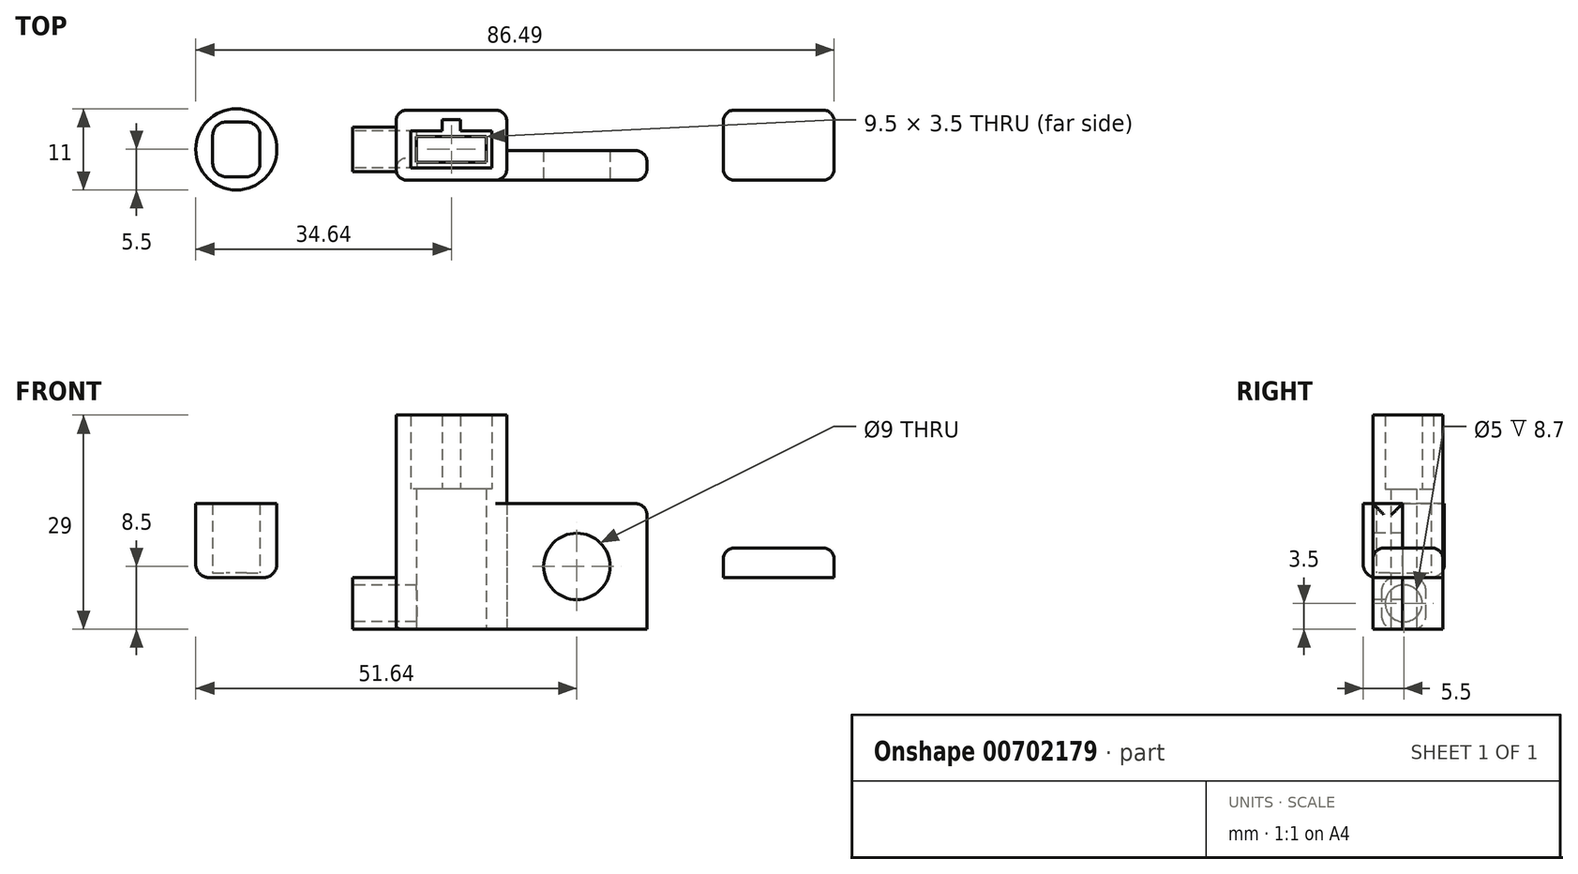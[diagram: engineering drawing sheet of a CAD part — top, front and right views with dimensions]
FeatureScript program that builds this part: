
annotation { "Feature Type Name" : "Feature", "Feature Type Description" : "" }
export const myFeature = defineFeature(function(context is Context, id is Id, definition is map)
    precondition{}
    {
        {
            var Q0;
            Q0=qCreatedBy(makeId("Top.planeOp"),FACE);
            var sketch = newSketch(context, id + "F0", { "sketchPlane" : qUnion([Q0])});
            skPoint(sketch, "E0.middle", {"position": v(0, 0) * mm});
            skLineSegment(sketch, "E1.bottom", {"start": v(5.5, -2.5) * mm, "end": v(-5.5, -2.5) * mm});
            skLineSegment(sketch, "E1.top", {"start": v(5.5, 2.5) * mm, "end": v(1.25, 2.5) * mm});
            skLineSegment(sketch, "E1.left", {"start": v(5.5, -2.5) * mm, "end": v(5.5, 2.5) * mm});
            skLineSegment(sketch, "E1.right", {"start": v(-5.5, -2.5) * mm, "end": v(-5.5, 2.5) * mm});
            skLineSegment(sketch, "E2.top", {"start": v(1.25, 4.01) * mm, "end": v(-1.25, 4.01) * mm});
            skLineSegment(sketch, "E2.left", {"start": v(1.25, 2.5) * mm, "end": v(1.25, 4.01) * mm});
            skLineSegment(sketch, "E2.right", {"start": v(-1.25, 2.5) * mm, "end": v(-1.25, 4.01) * mm});
            skPoint(sketch, "E2.middle", {"position": v(0, 3.26) * mm});
            skPoint(sketch, "E2.middle.positionSnap0", {"position": v(0, 2.5) * mm});
            skPoint(sketch, "E2.centerSnap0", {"position": v(0, 2.5) * mm});
            skLineSegment(sketch, "E3.bottom", {"start": v(7.5, -4.18) * mm, "end": v(-7.5, -4.18) * mm});
            skLineSegment(sketch, "E3.top", {"start": v(7.5, 5.32) * mm, "end": v(-7.5, 5.32) * mm});
            skLineSegment(sketch, "E3.left", {"start": v(7.5, -4.18) * mm, "end": v(7.5, 5.32) * mm});
            skLineSegment(sketch, "E3.right", {"start": v(-7.5, -4.18) * mm, "end": v(-7.5, 5.32) * mm});
            skPoint(sketch, "E3.middle", {"position": v(0, 0.57) * mm});
            skLineSegment(sketch, "E4.trimOffspring", {"start": v(-1.25, 2.5) * mm, "end": v(-5.5, 2.5) * mm});
            skLineSegment(sketch, "E5.bottom", {"start": v(4.75, -1.75) * mm, "end": v(-4.75, -1.75) * mm});
            skLineSegment(sketch, "E5.top", {"start": v(4.75, 1.75) * mm, "end": v(-4.75, 1.75) * mm});
            skLineSegment(sketch, "E5.left", {"start": v(4.75, -1.75) * mm, "end": v(4.75, 1.75) * mm});
            skLineSegment(sketch, "E5.right", {"start": v(-4.75, -1.75) * mm, "end": v(-4.75, 1.75) * mm});
            skLineSegment(sketch, "E6.bottom", {"start": v(7.5, -4.18) * mm, "end": v(26.5, -4.18) * mm});
            skLineSegment(sketch, "E6.top", {"start": v(7.5, -0.18) * mm, "end": v(26.5, -0.18) * mm});
            skLineSegment(sketch, "E6.left", {"start": v(7.5, -4.18) * mm, "end": v(7.5, -0.18) * mm});
            skLineSegment(sketch, "E6.right", {"start": v(26.5, -4.18) * mm, "end": v(26.5, -0.18) * mm});
            skLineSegment(sketch, "E7.bottom", {"start": v(-7.5, 3) * mm, "end": v(-13.37, 3) * mm});
            skLineSegment(sketch, "E7.top", {"start": v(-7.5, -3) * mm, "end": v(-13.37, -3) * mm});
            skLineSegment(sketch, "E7.left", {"start": v(-7.5, 3) * mm, "end": v(-7.5, -3) * mm});
            skLineSegment(sketch, "E7.right", {"start": v(-13.37, 3) * mm, "end": v(-13.37, -3) * mm});
            skPoint(sketch, "E7.middle", {"position": v(-10.43, 0) * mm});
            skSolve(sketch);
        }
        {
            var Q0;
            Q0=makeQuery(id+"F0.imprint","IMPRINT",FACE,{"disambiguationData":[TD([[makeQuery(id+"F0.imprint","IMPRINT",EDGE,{"derivedFrom":sQuery(id+"F0.wireOp",EDGE,"E1.bottom")}),1.0]])]});
            extrude(context, id + "F1", {"entities" : qUnion([Q0]), "depth" : 22 * mm, "offsetDistance" : 25 * mm});
        }
        {
            var Q0;
            Q0=makeQuery(id+"F0.imprint","IMPRINT",FACE,{"disambiguationData":[TD([[makeQuery(id+"F0.imprint","IMPRINT",EDGE,{"derivedFrom":sQuery(id+"F0.wireOp",EDGE,"E1.bottom")}),-1.0]])]});
            extrude(context, id + "F2", {"entities" : qUnion([Q0]), "operationType" : NewBodyOperationType.ADD, "depth" : 12 * mm, "offsetDistance" : 25 * mm});
        }
        {
            var Q0;
            Q0=makeQuery(id+"F0.imprint","IMPRINT",FACE,{"disambiguationData":[TD([[makeQuery(id+"F0.imprint","IMPRINT",EDGE,{"derivedFrom":sQuery(id+"F0.wireOp",EDGE,"E6.bottom")}),1.0]])]});
            extrude(context, id + "F3", {"entities" : qUnion([Q0]), "operationType" : NewBodyOperationType.ADD, "depth" : 10 * mm, "offsetDistance" : 25 * mm});
        }
        {
            var Q0;
            {var subQ0=sQuery(id+"F0.wireOp",EDGE,"E6.left");var subQ1=sQuery(id+"F0.wireOp",EDGE,"E4.trimOffspring");var subQ2=sQuery(id+"F0.wireOp",EDGE,"E2.right");var subQ3=sQuery(id+"F0.wireOp",EDGE,"E2.left");var subQ4=sQuery(id+"F0.wireOp",EDGE,"E2.top");var subQ5=sQuery(id+"F0.wireOp",EDGE,"E1.right");var subQ6=sQuery(id+"F0.wireOp",EDGE,"E1.left");var subQ7=sQuery(id+"F0.wireOp",EDGE,"E1.top");var subQ8=sQuery(id+"F0.wireOp",EDGE,"E1.bottom");Q0=makeQuery(id+"F3.boolean.opBoolean","MERGE",FACE,{"derivedFrom":[makeQuery(id+"F2.boolean.opBoolean","MERGE",FACE,{"derivedFrom":[makeQuery(id+"F1.opExtrude","CAP_FACE",FACE,{"disambiguationData":[OSD([subQ8,subQ7,subQ6,subQ5,subQ4,subQ3,subQ2,sQuery(id+"F0.wireOp",EDGE,"E3.bottom"),sQuery(id+"F0.wireOp",EDGE,"E3.top"),sQuery(id+"F0.wireOp",EDGE,"E3.left"),sQuery(id+"F0.wireOp",EDGE,"E3.right"),subQ1,subQ0])],"isStart":true}),makeQuery(id+"F2.opExtrude","CAP_FACE",FACE,{"disambiguationData":[OSD([subQ8,subQ7,subQ6,subQ5,subQ4,subQ3,subQ2,subQ1,sQuery(id+"F0.wireOp",EDGE,"E5.bottom"),sQuery(id+"F0.wireOp",EDGE,"E5.top"),sQuery(id+"F0.wireOp",EDGE,"E5.left"),sQuery(id+"F0.wireOp",EDGE,"E5.right")])],"isStart":true})]}),makeQuery(id+"F3.opExtrude","CAP_FACE",FACE,{"disambiguationData":[OSD([sQuery(id+"F0.wireOp",EDGE,"E6.bottom"),sQuery(id+"F0.wireOp",EDGE,"E6.top"),subQ0,sQuery(id+"F0.wireOp",EDGE,"E6.right")])],"isStart":true})]});}
            extrude(context, id + "F4", {"entities" : qUnion([Q0]), "operationType" : NewBodyOperationType.ADD, "depth" : 7 * mm, "offsetDistance" : 25 * mm});
        }
        {
            var Q0;
            Q0=makeQuery(id+"F3.boolean.opBoolean","MERGE",FACE,{"derivedFrom":[makeQuery(id+"F1.opExtrude","SWEPT_FACE",FACE,{"disambiguationData":[OSD([sQuery(id+"F0.wireOp",EDGE,"E3.bottom")])]}),makeQuery(id+"F3.opExtrude","SWEPT_FACE",FACE,{"disambiguationData":[OSD([sQuery(id+"F0.wireOp",EDGE,"E6.bottom")])]})]});
            var sketch = newSketch(context, id + "F5", { "sketchPlane" : qUnion([Q0])});
            skCircle(sketch, "E8", {"center": v(17, 1.5) * mm, "radius": 4.5 * mm});
            skPoint(sketch, "E8.centerSnap0", {"position": v(17, 10) * mm});
            skPoint(sketch, "E8.centerSnap1", {"position": v(23, 1.5) * mm});
            skPoint(sketch, "E9", {"position": v(26.5, 1.5) * mm});
            skSolve(sketch);
        }
        {
            var Q0;
            Q0=makeQuery(id+"F5.imprint","IMPRINT",FACE,{"disambiguationData":[TD([[makeQuery(id+"F5.imprint","IMPRINT",EDGE,{"derivedFrom":sQuery(id+"F5.wireOp",EDGE,"E8")}),1.0]])]});
            extrude(context, id + "F6", {"entities" : qUnion([Q0]), "operationType" : NewBodyOperationType.REMOVE, "oppositeDirection" : true, "depth" : 25 * mm, "offsetDistance" : 25 * mm});
        }
        {
            var Q0;
            Q0=makeQuery(id+"F0.imprint","IMPRINT",FACE,{"disambiguationData":[TD([[makeQuery(id+"F0.imprint","IMPRINT",EDGE,{"derivedFrom":sQuery(id+"F0.wireOp",EDGE,"E7.bottom")}),1.0]])]});
            extrude(context, id + "F7", {"entities" : qUnion([Q0]), "operationType" : NewBodyOperationType.ADD, "oppositeDirection" : true, "depth" : 7 * mm, "offsetDistance" : 25 * mm});
        }
        {
            var Q0;
            Q0=makeQuery(id+"F1.opExtrude","SWEPT_EDGE",EDGE,{"disambiguationData":[OSD([sQuery(id+"F0.wireOp",EDGE,"E3.top"),sQuery(id+"F0.wireOp",EDGE,"E3.right")])]});
            var Q1;
            Q1=makeQuery(id+"F1.opExtrude","SWEPT_EDGE",EDGE,{"disambiguationData":[OSD([sQuery(id+"F0.wireOp",EDGE,"E3.top"),sQuery(id+"F0.wireOp",EDGE,"E3.left")])]});
            var Q2;
            Q2=makeQuery(id+"F1.opExtrude","SWEPT_EDGE",EDGE,{"disambiguationData":[OSD([sQuery(id+"F0.wireOp",EDGE,"E3.bottom"),sQuery(id+"F0.wireOp",EDGE,"E3.left")])]});
            var Q3;
            Q3=makeQuery(id+"F1.opExtrude","SWEPT_EDGE",EDGE,{"disambiguationData":[OSD([sQuery(id+"F0.wireOp",EDGE,"E3.bottom"),sQuery(id+"F0.wireOp",EDGE,"E3.right")])]});
            var Q4;
            Q4=makeQuery(id+"F1.opExtrude","SWEPT_EDGE",EDGE,{"disambiguationData":[OSD([sQuery(id+"F0.wireOp",EDGE,"E3.bottom"),sQuery(id+"F0.wireOp",EDGE,"E6.bottom"),sQuery(id+"F0.wireOp",EDGE,"E6.left")])]});
            var Q5;
            Q5=makeQuery(id+"F3.opExtrude","SWEPT_EDGE",EDGE,{"disambiguationData":[OSD([sQuery(id+"F0.wireOp",EDGE,"E6.bottom"),sQuery(id+"F0.wireOp",EDGE,"E6.right")])]});
            var Q6;
            Q6=makeQuery(id+"F3.opExtrude","SWEPT_EDGE",EDGE,{"disambiguationData":[OSD([sQuery(id+"F0.wireOp",EDGE,"E6.top"),sQuery(id+"F0.wireOp",EDGE,"E6.right")])]});
            var Q7;
            Q7=makeQuery(id+"F3.opExtrude","SWEPT_EDGE",EDGE,{"disambiguationData":[OSD([sQuery(id+"F0.wireOp",EDGE,"E3.left"),sQuery(id+"F0.wireOp",EDGE,"E6.top"),sQuery(id+"F0.wireOp",EDGE,"E6.left")])]});
            var Q8;
            Q8=makeQuery(id+"F3.opExtrude","CAP_EDGE",EDGE,{"disambiguationData":[OSD([sQuery(id+"F0.wireOp",EDGE,"E6.right")])],"isStart":false});
            fillet(context, id + "F8", {"entities" : qUnion([Q0, Q1, Q2, Q3, Q4, Q5, Q6, Q7, Q8]), "radius" : 1.5 * mm, "tangentPropagation" : true, "allowEdgeOverflow" : false});
        }
        {
            var Q0;
            Q0=makeQuery(id+"F7.opExtrude","CAP_EDGE",EDGE,{"disambiguationData":[OSD([sQuery(id+"F0.wireOp",EDGE,"E7.bottom")])],"isStart":false});
            var Q1;
            Q1=makeQuery(id+"F7.opExtrude","CAP_EDGE",EDGE,{"disambiguationData":[OSD([sQuery(id+"F0.wireOp",EDGE,"E7.top")])],"isStart":false});
            var Q2;
            Q2=makeQuery(id+"F7.opExtrude","CAP_EDGE",EDGE,{"disambiguationData":[OSD([sQuery(id+"F0.wireOp",EDGE,"E7.top")])],"isStart":true});
            var Q3;
            Q3=makeQuery(id+"F7.opExtrude","CAP_EDGE",EDGE,{"disambiguationData":[OSD([sQuery(id+"F0.wireOp",EDGE,"E7.bottom")])],"isStart":true});
            fillet(context, id + "F9", {"entities" : qUnion([Q0, Q1, Q2, Q3]), "radius" : 1.8 * mm, "tangentPropagation" : true, "allowEdgeOverflow" : false});
        }
        {
            var Q0;
            Q0=makeQuery(id+"F7.opExtrude","SWEPT_FACE",FACE,{"disambiguationData":[OSD([sQuery(id+"F0.wireOp",EDGE,"E7.right")])]});
            var sketch = newSketch(context, id + "F10", { "sketchPlane" : qUnion([Q0])});
            skCircle(sketch, "E10", {"center": v(0, -3.5) * mm, "radius": 2.5 * mm});
            skPoint(sketch, "E10.centerSnap0", {"position": v(3, -3.5) * mm});
            skPoint(sketch, "E10.centerSnap1", {"position": v(0, -7) * mm});
            skSolve(sketch);
        }
        {
            var Q0;
            Q0=makeQuery(id+"F10.imprint","IMPRINT",FACE,{"disambiguationData":[TD([[makeQuery(id+"F10.imprint","IMPRINT",EDGE,{"derivedFrom":sQuery(id+"F10.wireOp",EDGE,"E10")}),1.0]])]});
            extrude(context, id + "F11", {"entities" : qUnion([Q0]), "operationType" : NewBodyOperationType.REMOVE, "oppositeDirection" : true, "depth" : 8.7 * mm, "offsetDistance" : 25 * mm});
        }
        {
            var Q0;
            Q0=qCreatedBy(makeId("Top.planeOp"),FACE);
            var sketch = newSketch(context, id + "F12", { "sketchPlane" : qUnion([Q0])});
            skLineSegment(sketch, "E11.bottom", {"start": v(-25.94, -3.7) * mm, "end": v(-32.34, -3.7) * mm});
            skLineSegment(sketch, "E11.top", {"start": v(-25.94, 3.7) * mm, "end": v(-32.34, 3.7) * mm});
            skLineSegment(sketch, "E11.left", {"start": v(-25.94, -3.7) * mm, "end": v(-25.94, 3.7) * mm});
            skLineSegment(sketch, "E11.right", {"start": v(-32.34, -3.7) * mm, "end": v(-32.34, 3.7) * mm});
            skPoint(sketch, "E11.middle", {"position": v(-29.14, 0) * mm});
            skCircle(sketch, "E12", {"center": v(-29.14, 0) * mm, "radius": 5.5 * mm});
            skSolve(sketch);
        }
        {
            var Q0;
            Q0=makeQuery(id+"F12.imprint","IMPRINT",FACE,{"disambiguationData":[TD([[makeQuery(id+"F12.imprint","IMPRINT",EDGE,{"derivedFrom":sQuery(id+"F12.wireOp",EDGE,"E11.bottom")}),1.0]])]});
            extrude(context, id + "F13", {"entities" : qUnion([Q0]), "depth" : 10 * mm, "offsetDistance" : 25 * mm});
        }
        {
            var Q0;
            Q0=makeQuery(id+"F12.imprint","IMPRINT",FACE,{"disambiguationData":[TD([[makeQuery(id+"F12.imprint","IMPRINT",EDGE,{"derivedFrom":sQuery(id+"F12.wireOp",EDGE,"E11.bottom")}),-1.0]])]});
            extrude(context, id + "F14", {"entities" : qUnion([Q0]), "operationType" : NewBodyOperationType.ADD, "depth" : 0.6 * mm, "offsetDistance" : 25 * mm});
        }
        {
            var Q0;
            Q0=makeQuery(id+"F13.opExtrude","SWEPT_EDGE",EDGE,{"disambiguationData":[OSD([sQuery(id+"F12.wireOp",EDGE,"E11.top"),sQuery(id+"F12.wireOp",EDGE,"E11.left")])]});
            var Q1;
            Q1=makeQuery(id+"F13.opExtrude","SWEPT_EDGE",EDGE,{"disambiguationData":[OSD([sQuery(id+"F12.wireOp",EDGE,"E11.top"),sQuery(id+"F12.wireOp",EDGE,"E11.right")])]});
            var Q2;
            Q2=makeQuery(id+"F13.opExtrude","CAP_EDGE",EDGE,{"disambiguationData":[OSD([sQuery(id+"F12.wireOp",EDGE,"E12")])],"isStart":true});
            var Q3;
            Q3=makeQuery(id+"F13.opExtrude","SWEPT_EDGE",EDGE,{"disambiguationData":[OSD([sQuery(id+"F12.wireOp",EDGE,"E11.bottom"),sQuery(id+"F12.wireOp",EDGE,"E11.left")])]});
            var Q4;
            Q4=makeQuery(id+"F13.opExtrude","SWEPT_EDGE",EDGE,{"disambiguationData":[OSD([sQuery(id+"F12.wireOp",EDGE,"E11.bottom"),sQuery(id+"F12.wireOp",EDGE,"E11.right")])]});
            fillet(context, id + "F15", {"entities" : qUnion([Q0, Q1, Q2, Q3, Q4]), "radius" : 1.8 * mm, "tangentPropagation" : true, "allowEdgeOverflow" : false});
        }
        {
            var Q0;
            Q0=qCreatedBy(makeId("Top.planeOp"),FACE);
            var sketch = newSketch(context, id + "F16", { "sketchPlane" : qUnion([Q0])});
            skLineSegment(sketch, "E13.bottom", {"start": v(51.85, -4.18) * mm, "end": v(36.85, -4.18) * mm});
            skLineSegment(sketch, "E13.top", {"start": v(51.85, 5.32) * mm, "end": v(36.85, 5.32) * mm});
            skLineSegment(sketch, "E13.left", {"start": v(51.85, -4.18) * mm, "end": v(51.85, 5.32) * mm});
            skLineSegment(sketch, "E13.right", {"start": v(36.85, -4.18) * mm, "end": v(36.85, 5.32) * mm});
            skLineSegment(sketch, "E14.left", {"start": v(51.85, -4.18) * mm, "end": v(51.85, -0.18) * mm});
            skLineSegment(sketch, "E15.left", {"start": v(36.85, 3) * mm, "end": v(36.85, -3) * mm});
            skPoint(sketch, "E15.middle", {"position": v(33.92, 0) * mm});
            skSolve(sketch);
        }
        {
            var Q0;
            {var subQ1=sQuery(id+"F16.wireOp",EDGE,"E13.bottom");Q0=makeQuery(id+"F16.imprint","IMPRINT",FACE,{"disambiguationData":[TD([[makeQuery(id+"F16.imprint","IMPRINT",EDGE,{"derivedFrom":subQ1}),-1.0]])]});}
            extrude(context, id + "F17", {"entities" : qUnion([Q0]), "depth" : 4 * mm, "offsetDistance" : 25 * mm});
        }
        {
            var Q0;
            Q0=makeQuery(id+"F17.opExtrude","SWEPT_EDGE",EDGE,{"disambiguationData":[OSD([sQuery(id+"F16.wireOp",EDGE,"E13.bottom"),sQuery(id+"F16.wireOp",EDGE,"E14.left")])]});
            var Q1;
            Q1=makeQuery(id+"F17.opExtrude","SWEPT_EDGE",EDGE,{"disambiguationData":[OSD([sQuery(id+"F16.wireOp",EDGE,"E13.bottom"),sQuery(id+"F16.wireOp",EDGE,"E13.right")])]});
            var Q2;
            Q2=makeQuery(id+"F17.opExtrude","SWEPT_EDGE",EDGE,{"disambiguationData":[OSD([sQuery(id+"F16.wireOp",EDGE,"E13.top"),sQuery(id+"F16.wireOp",EDGE,"E13.right")])]});
            var Q3;
            Q3=makeQuery(id+"F17.opExtrude","SWEPT_EDGE",EDGE,{"disambiguationData":[OSD([sQuery(id+"F16.wireOp",EDGE,"E13.top"),sQuery(id+"F16.wireOp",EDGE,"E13.left")])]});
            var Q4;
            Q4=makeQuery(id+"F17.opExtrude","CAP_FACE",FACE,{"disambiguationData":[OSD([sQuery(id+"F16.wireOp",EDGE,"E13.bottom"),sQuery(id+"F16.wireOp",EDGE,"E13.top"),sQuery(id+"F16.wireOp",EDGE,"E13.left"),sQuery(id+"F16.wireOp",EDGE,"E13.right"),sQuery(id+"F16.wireOp",EDGE,"E14.left"),sQuery(id+"F16.wireOp",EDGE,"E15.left")])],"isStart":false});
            fillet(context, id + "F18", {"entities" : qUnion([Q0, Q1, Q2, Q3, Q4]), "radius" : 1.5 * mm, "tangentPropagation" : true, "allowEdgeOverflow" : false});
        }
    });
